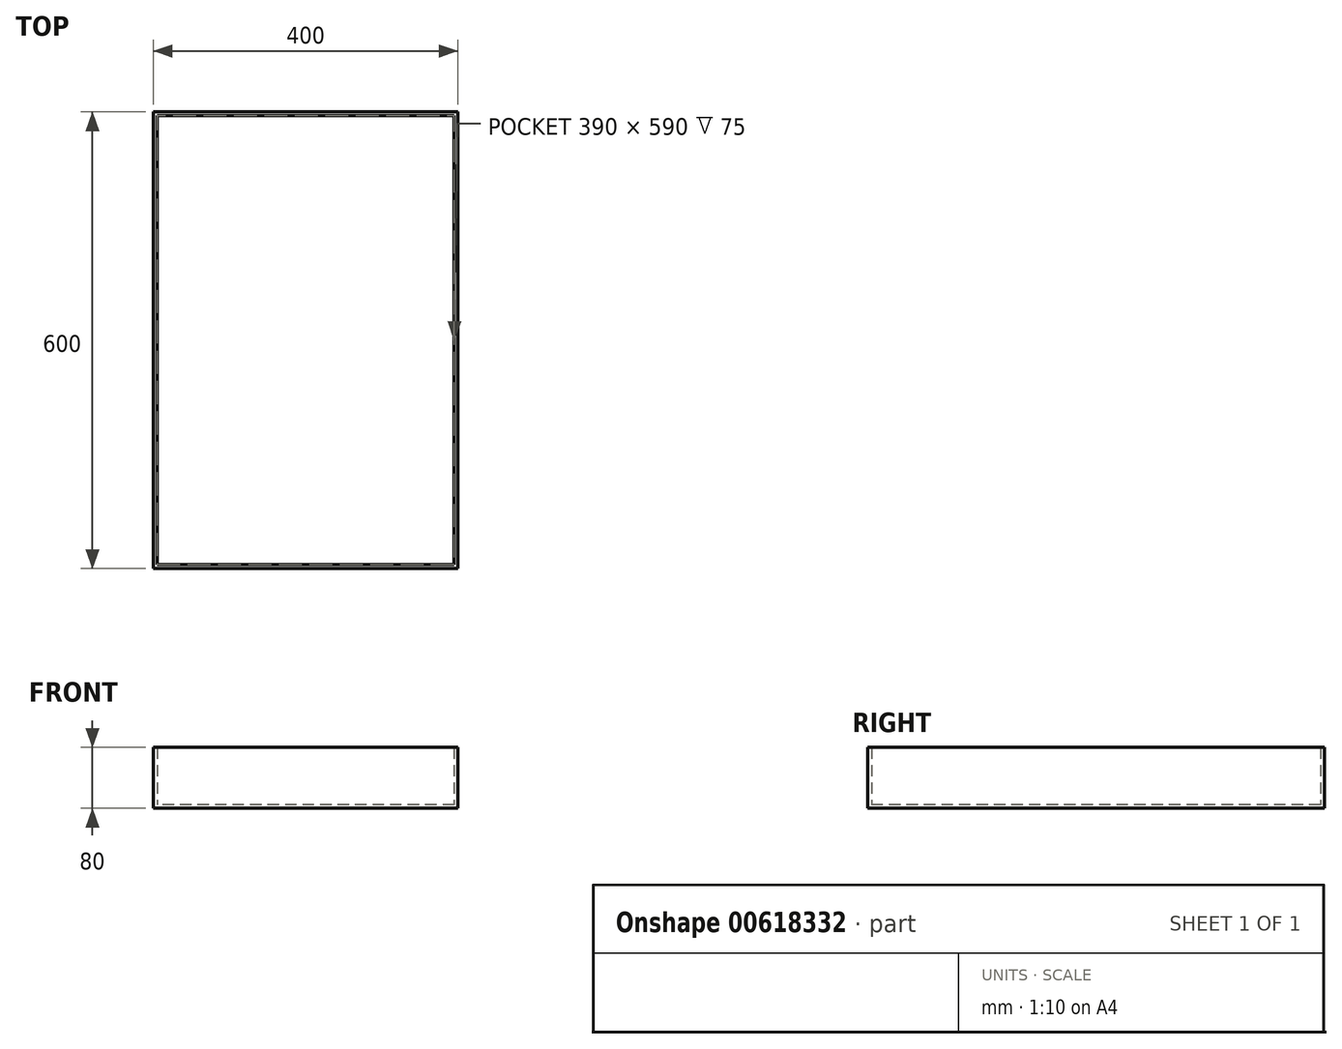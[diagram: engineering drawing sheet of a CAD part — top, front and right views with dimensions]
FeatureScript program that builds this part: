
annotation { "Feature Type Name" : "Feature", "Feature Type Description" : "" }
export const myFeature = defineFeature(function(context is Context, id is Id, definition is map)
    precondition{}
    {
        {
            var Q0;
            Q0=qCreatedBy(makeId("Top.planeOp"),FACE);
            var sketch = newSketch(context, id + "F0", { "sketchPlane" : qUnion([Q0])});
            skLineSegment(sketch, "E0.bottom", {"start": v(200, 300) * mm, "end": v(-200, 300) * mm});
            skLineSegment(sketch, "E0.top", {"start": v(200, -300) * mm, "end": v(-200, -300) * mm});
            skLineSegment(sketch, "E0.left", {"start": v(200, 300) * mm, "end": v(200, -300) * mm});
            skLineSegment(sketch, "E0.right", {"start": v(-200, 300) * mm, "end": v(-200, -300) * mm});
            skPoint(sketch, "E0.middle", {"position": v(0, 0) * mm});
            skSolve(sketch);
        }
        {
            var Q0;
            Q0=makeQuery(id+"F0.imprint","IMPRINT",FACE,{"disambiguationData":[TD([[makeQuery(id+"F0.imprint","IMPRINT",EDGE,{"derivedFrom":sQuery(id+"F0.wireOp",EDGE,"E0.bottom")}),1.0]])]});
            extrude(context, id + "F1", {"entities" : qUnion([Q0]), "depth" : 80 * mm, "offsetDistance" : 25 * mm});
        }
        {
            var Q0;
            Q0=makeQuery(id+"F1.opExtrude","CAP_FACE",FACE,{"disambiguationData":[OSD([sQuery(id+"F0.wireOp",EDGE,"E0.bottom"),sQuery(id+"F0.wireOp",EDGE,"E0.top"),sQuery(id+"F0.wireOp",EDGE,"E0.left"),sQuery(id+"F0.wireOp",EDGE,"E0.right")])],"isStart":false});
            shell(context, id + "F2", {"entities" : qUnion([Q0]), "thickness" : 5 * mm});
        }
        {
            var Q0;
            Q0=makeQuery(id+"F1.opExtrude","SWEPT_BODY",BODY,{"disambiguationData":[OSD([sQuery(id+"F0.wireOp",EDGE,"E0.bottom"),sQuery(id+"F0.wireOp",EDGE,"E0.top"),sQuery(id+"F0.wireOp",EDGE,"E0.left"),sQuery(id+"F0.wireOp",EDGE,"E0.right")])]});
            transform(context, id + "F3", {"entities" : qUnion([Q0]), "transformType" : TransformType.TRANSLATION_3D, "dx" : 0 * mm, "dy" : 0 * mm, "dz" : 90 * mm, "makeCopy" : true});
        }
        {
            var Q0;
            Q0=makeQuery(id+"F3.opPattern","COPY",BODY,{"derivedFrom":makeQuery(id+"F1.opExtrude","SWEPT_BODY",BODY,{"disambiguationData":[OSD([sQuery(id+"F0.wireOp",EDGE,"E0.bottom"),sQuery(id+"F0.wireOp",EDGE,"E0.top"),sQuery(id+"F0.wireOp",EDGE,"E0.left"),sQuery(id+"F0.wireOp",EDGE,"E0.right")])]}),"instanceName":"1"});
            deleteBodies(context, id + "F4", {"entities" : qUnion([Q0])});
        }
    });
